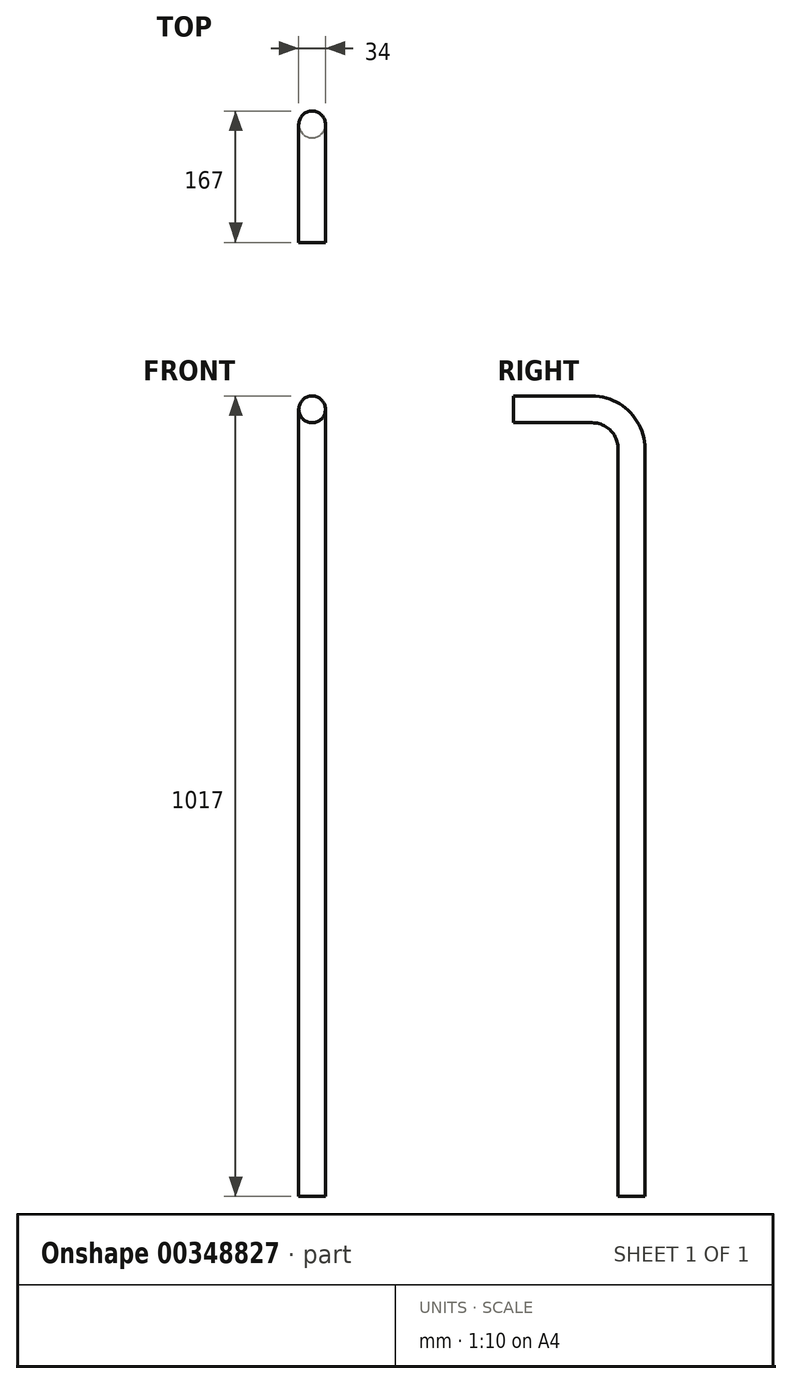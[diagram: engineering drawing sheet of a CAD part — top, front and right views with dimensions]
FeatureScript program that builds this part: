
annotation { "Feature Type Name" : "Feature", "Feature Type Description" : "" }
export const myFeature = defineFeature(function(context is Context, id is Id, definition is map)
    precondition{}
    {
        {
            var Q0;
            Q0=qCreatedBy(makeId("Right.planeOp"),FACE);
            var sketch = newSketch(context, id + "F0", { "sketchPlane" : qUnion([Q0])});
            skLineSegment(sketch, "E0", {"start": v(0, 0) * mm, "end": v(0, 950) * mm});
            skLineSegment(sketch, "E1", {"start": v(-50, 1000) * mm, "end": v(-150, 1000) * mm});
            skPoint(sketch, "E2.visualSharp", {"position": v(0, 1000) * mm});
            skArc(sketch, "E2.filletArc", {"start": v(0, 950) * mm, "mid": v(-14.64, 985.36) * mm, "end": v(-50, 1000) * mm});
            skLineSegment(sketch, "E3", {"start": v(0, 0) * mm, "end": v(-175.78, 0) * mm, "construction": true});
            skLineSegment(sketch, "E4", {"start": v(-150, 1000) * mm, "end": v(-150, -521.87) * mm, "construction": true});
            skSolve(sketch);
        }
        {
            var Q0;
            Q0=qCreatedBy(makeId("Top.planeOp"),FACE);
            var sketch = newSketch(context, id + "F1", { "sketchPlane" : qUnion([Q0])});
            skCircle(sketch, "E5", {"center": v(0, 0) * mm, "radius": 17 * mm});
            skSolve(sketch);
        }
        {
            var Q0;
            Q0=makeQuery(id+"F1.imprint","IMPRINT",FACE,{"disambiguationData":[TD([[makeQuery(id+"F1.imprint","IMPRINT",EDGE,{"derivedFrom":sQuery(id+"F1.wireOp",EDGE,"E5")}),1.0]])]});
            var Q1;
            Q1=sQuery(id+"F0.wireOp",EDGE,"E0");
            var Q2;
            Q2=sQuery(id+"F0.wireOp",EDGE,"E2.filletArc");
            var Q3;
            Q3=sQuery(id+"F0.wireOp",EDGE,"E1");
            sweep(context, id + "F2", {"profiles" : qUnion([Q0]), "path" : qUnion([Q1, Q2, Q3])});
        }
    });
